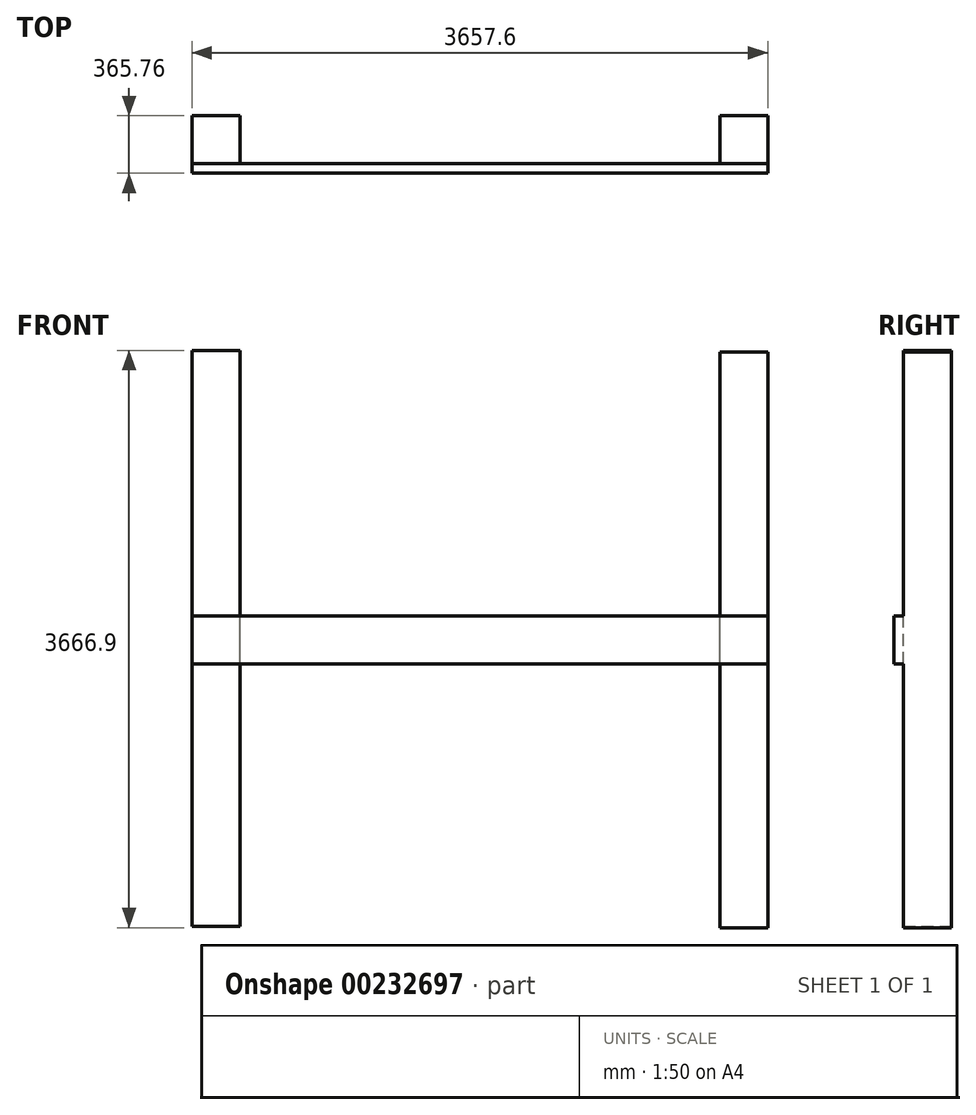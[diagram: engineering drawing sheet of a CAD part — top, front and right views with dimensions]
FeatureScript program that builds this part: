
annotation { "Feature Type Name" : "Feature", "Feature Type Description" : "" }
export const myFeature = defineFeature(function(context is Context, id is Id, definition is map)
    precondition{}
    {
        {
            var Q0;
            Q0=qCreatedBy(makeId("Front.planeOp"),FACE);
            var sketch = newSketch(context, id + "F0", { "sketchPlane" : qUnion([Q0])});
            skLineSegment(sketch, "E0.bottom", {"start": v(152.4, -1828.8) * mm, "end": v(-152.4, -1828.8) * mm});
            skLineSegment(sketch, "E0.top", {"start": v(152.4, 1828.8) * mm, "end": v(-152.4, 1828.8) * mm});
            skLineSegment(sketch, "E0.left", {"start": v(152.4, -1828.8) * mm, "end": v(152.4, 1828.8) * mm});
            skLineSegment(sketch, "E0.right", {"start": v(-152.4, -1828.8) * mm, "end": v(-152.4, 1828.8) * mm});
            skPoint(sketch, "E0.middle", {"position": v(0, 0) * mm});
            skSolve(sketch);
        }
        {
            var Q0;
            Q0=makeQuery(id+"F0.imprint","IMPRINT",FACE,{"disambiguationData":[TD([[makeQuery(id+"F0.imprint","IMPRINT",EDGE,{"derivedFrom":sQuery(id+"F0.wireOp",EDGE,"E0.bottom")}),-1.0]])]});
            extrude(context, id + "F1", {"entities" : qUnion([Q0]), "depth" : 304.8 * mm});
        }
        {
            var Q0;
            Q0=makeQuery(id+"F1.opExtrude","CAP_FACE",FACE,{"disambiguationData":[OSD([sQuery(id+"F0.wireOp",EDGE,"E0.bottom"),sQuery(id+"F0.wireOp",EDGE,"E0.top"),sQuery(id+"F0.wireOp",EDGE,"E0.left"),sQuery(id+"F0.wireOp",EDGE,"E0.right")])],"isStart":false});
            var sketch = newSketch(context, id + "F2", { "sketchPlane" : qUnion([Q0])});
            skLineSegment(sketch, "E1.bottom", {"start": v(-152.4, 143.1) * mm, "end": v(3505.2, 143.1) * mm});
            skLineSegment(sketch, "E1.top", {"start": v(-152.4, -161.7) * mm, "end": v(3505.2, -161.7) * mm});
            skLineSegment(sketch, "E1.left", {"start": v(-152.4, 143.1) * mm, "end": v(-152.4, -161.7) * mm});
            skLineSegment(sketch, "E1.right", {"start": v(3505.2, 143.1) * mm, "end": v(3505.2, -161.7) * mm});
            skSolve(sketch);
        }
        {
            var Q0;
            {var subQ0=sQuery(id+"F2.wireOp",EDGE,"E1.left");Q0=makeQuery(id+"F2.imprint","IMPRINT",FACE,{"disambiguationData":[TD([[makeQuery(id+"F2.imprint","IMPRINT",EDGE,{"derivedFrom":subQ0}),-1.0]])]});}
            var Q1;
            {var subQ0=sQuery(id+"F2.wireOp",EDGE,"E1.right");Q1=makeQuery(id+"F2.imprint","IMPRINT",FACE,{"disambiguationData":[TD([[makeQuery(id+"F2.imprint","IMPRINT",EDGE,{"derivedFrom":subQ0}),-1.0]])]});}
            extrude(context, id + "F3", {"entities" : qUnion([Q0, Q1]), "operationType" : NewBodyOperationType.ADD, "depth" : 60.96 * mm});
        }
        {
            var Q0;
            Q0=makeQuery(id+"F3.opExtrude","CAP_FACE",FACE,{"disambiguationData":[OSD([sQuery(id+"F2.wireOp",EDGE,"E1.bottom"),sQuery(id+"F2.wireOp",EDGE,"E1.top"),sQuery(id+"F2.wireOp",EDGE,"E1.left"),sQuery(id+"F2.wireOp",EDGE,"E1.right")])],"isStart":true});
            var sketch = newSketch(context, id + "F4", { "sketchPlane" : qUnion([Q0])});
            skLineSegment(sketch, "E2.bottom", {"start": v(-3505.2, -161.7) * mm, "end": v(-3200.4, -161.7) * mm});
            skLineSegment(sketch, "E2.top", {"start": v(-3505.2, -1838.1) * mm, "end": v(-3200.4, -1838.1) * mm});
            skLineSegment(sketch, "E2.left", {"start": v(-3505.2, -161.7) * mm, "end": v(-3505.2, -1838.1) * mm});
            skLineSegment(sketch, "E2.right", {"start": v(-3200.4, -161.7) * mm, "end": v(-3200.4, -1838.1) * mm});
            skLineSegment(sketch, "E3.top", {"start": v(-3505.2, 1819.5) * mm, "end": v(-3200.4, 1819.5) * mm});
            skLineSegment(sketch, "E3.left", {"start": v(-3505.2, -161.7) * mm, "end": v(-3505.2, 1819.5) * mm});
            skLineSegment(sketch, "E3.right", {"start": v(-3200.4, -161.7) * mm, "end": v(-3200.4, 1819.5) * mm});
            skSolve(sketch);
        }
        {
            var Q0;
            {var subQ0=sQuery(id+"F4.wireOp",EDGE,"E3.top");Q0=makeQuery(id+"F4.imprint","IMPRINT",FACE,{"disambiguationData":[TD([[makeQuery(id+"F4.imprint","IMPRINT",EDGE,{"derivedFrom":subQ0}),-1.0]])]});}
            var Q1;
            {var subQ0=sQuery(id+"F4.wireOp",EDGE,"E2.bottom");Q1=makeQuery(id+"F4.imprint","IMPRINT",FACE,{"disambiguationData":[TD([[makeQuery(id+"F4.imprint","IMPRINT",EDGE,{"derivedFrom":subQ0}),-1.0]])]});}
            var Q2;
            Q2=makeQuery(id+"F4.imprint","IMPRINT",FACE,{"disambiguationData":[TD([[makeQuery(id+"F4.imprint","IMPRINT",EDGE,{"derivedFrom":sQuery(id+"F4.wireOp",EDGE,"E2.top")}),1.0]])]});
            extrude(context, id + "F5", {"entities" : qUnion([Q0, Q1, Q2]), "operationType" : NewBodyOperationType.ADD, "depth" : 304.8 * mm});
        }
    });
